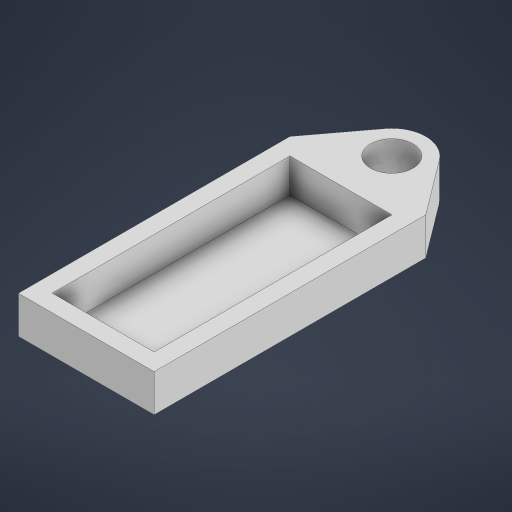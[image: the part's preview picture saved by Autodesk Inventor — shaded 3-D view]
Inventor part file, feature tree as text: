
AUTODESK INVENTOR PART (.ipt)
format: ipt  version: 2024.3 (Build 283343010, 343A)  size: 428,032 bytes
history: native  units: mm
features: extrude x2, sketch x1
ambient origin geometry x8: Origin, YZ Plane, XZ Plane, XY Plane, X Axis, Y Axis, Z Axis, Center Point
bodies: Volumenkörper1 (feature_tree)
feature tree (3):
  sketch  "Skizze1"  dims[d0=12.5mm d1=30.0mm d2=70.0mm d3=15.0mm d4=5.0mm d5=5.0mm d6=5.0mm d7=10.0mm d8=10.0mm d9=0.0mm d10=1.0mm d11=0.0mm]
  extrude  "Extrusion1"  Depth=30.0mm
  extrude  "Extrusion2"  Depth=70.0mm
